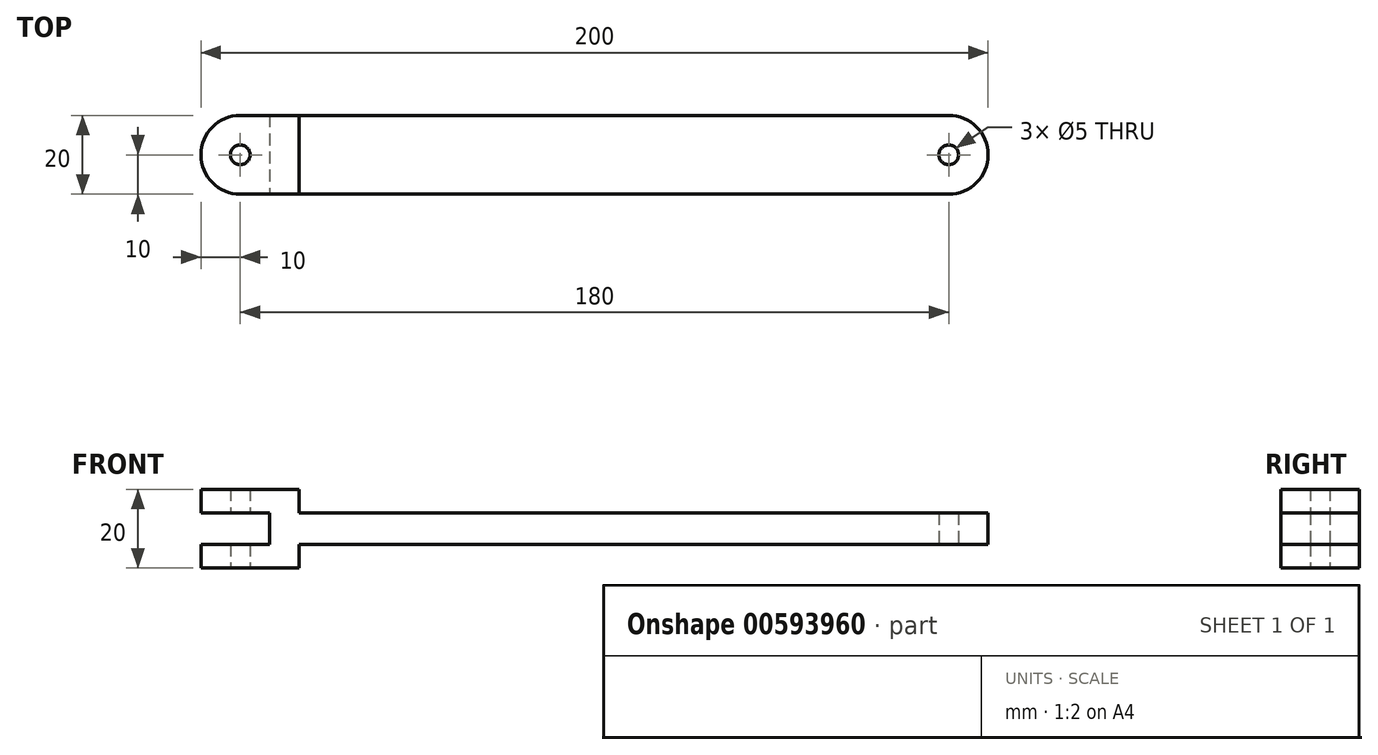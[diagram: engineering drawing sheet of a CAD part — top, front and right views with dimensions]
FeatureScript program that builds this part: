
annotation { "Feature Type Name" : "Feature", "Feature Type Description" : "" }
export const myFeature = defineFeature(function(context is Context, id is Id, definition is map)
    precondition{}
    {
        {
            var Q0;
            Q0=qCreatedBy(makeId("Top.planeOp"),FACE);
            var sketch = newSketch(context, id + "F0", { "sketchPlane" : qUnion([Q0])});
            skLineSegment(sketch, "E0.bottom", {"start": v(75, 10) * mm, "end": v(-75, 10) * mm});
            skLineSegment(sketch, "E0.top", {"start": v(75, -10) * mm, "end": v(-75, -10) * mm});
            skLineSegment(sketch, "E0.left", {"start": v(75, 10) * mm, "end": v(75, -10) * mm});
            skLineSegment(sketch, "E0.right", {"start": v(-75, 10) * mm, "end": v(-75, -10) * mm});
            skPoint(sketch, "E0.middle", {"position": v(0, 0) * mm});
            skCircle(sketch, "E1", {"center": v(90, 0) * mm, "radius": 10 * mm});
            skPoint(sketch, "E2", {"position": v(100, 0) * mm});
            skPoint(sketch, "E3", {"position": v(90, 10) * mm});
            skPoint(sketch, "E4", {"position": v(90, -10) * mm});
            skLineSegment(sketch, "E5", {"start": v(75, 10) * mm, "end": v(90, 10) * mm});
            skLineSegment(sketch, "E6", {"start": v(90, -10) * mm, "end": v(75, -10) * mm});
            skCircle(sketch, "E7", {"center": v(90, 0) * mm, "radius": 2.5 * mm});
            skCircle(sketch, "E8", {"center": v(-90, 0) * mm, "radius": 10 * mm});
            skPoint(sketch, "E9", {"position": v(-100, 0) * mm});
            skLineSegment(sketch, "E10", {"start": v(-90, 0) * mm, "end": v(-90, 10) * mm, "construction": true});
            skLineSegment(sketch, "E11", {"start": v(-90, 10) * mm, "end": v(-90, 0) * mm, "construction": true});
            skLineSegment(sketch, "E12", {"start": v(-90, -10) * mm, "end": v(-90, 0) * mm, "construction": true});
            skLineSegment(sketch, "E13", {"start": v(-90, 0) * mm, "end": v(-100, 0) * mm, "construction": true});
            skLineSegment(sketch, "E14", {"start": v(-90, 0) * mm, "end": v(-75, 0) * mm, "construction": true});
            skLineSegment(sketch, "E15", {"start": v(-90, 10) * mm, "end": v(-75, 10) * mm});
            skLineSegment(sketch, "E16", {"start": v(-90, -10) * mm, "end": v(-75, -10) * mm});
            skLineSegment(sketch, "E17", {"start": v(-75, -10) * mm, "end": v(-75, 10) * mm});
            skCircle(sketch, "E18", {"center": v(-90, 0) * mm, "radius": 2.5 * mm});
            skSolve(sketch);
        }
        {
            var Q0;
            Q0=makeQuery(id+"F0.imprint","IMPRINT",FACE,{"disambiguationData":[TD([[makeQuery(id+"F0.imprint","IMPRINT",EDGE,{"derivedFrom":sQuery(id+"F0.wireOp",EDGE,"E0.bottom")}),1.0]])]});
            var Q1;
            Q1=makeQuery(id+"F0.imprint","IMPRINT",FACE,{"disambiguationData":[TD([[makeQuery(id+"F0.imprint","IMPRINT",EDGE,{"derivedFrom":sQuery(id+"F0.wireOp",EDGE,"E0.left")}),1.0]])]});
            var Q2;
            Q2=makeQuery(id+"F0.imprint","IMPRINT",FACE,{"disambiguationData":[TD([[makeQuery(id+"F0.imprint","IMPRINT",EDGE,{"derivedFrom":sQuery(id+"F0.wireOp",EDGE,"E7")}),-1.0]])]});
            var Q3;
            Q3=makeQuery(id+"F0.imprint","IMPRINT",FACE,{"disambiguationData":[TD([[makeQuery(id+"F0.imprint","IMPRINT",EDGE,{"derivedFrom":sQuery(id+"F0.wireOp",EDGE,"5iIiheSA-0ZHN-F9So-mZuT-hha1FEnrlhel.bottom")}),1.0]])]});
            extrude(context, id + "F1", {"entities" : qUnion([Q0, Q1, Q2, Q3]), "endBound" : BoundingType.SYMMETRIC, "depth" : 8 * mm, "offsetDistance" : 25 * mm});
        }
        {
            var Q0;
            Q0=makeQuery(id+"F0.imprint","IMPRINT",FACE,{"disambiguationData":[TD([[makeQuery(id+"F0.imprint","IMPRINT",EDGE,{"derivedFrom":sQuery(id+"F0.wireOp",EDGE,"E18")}),-1.0]])]});
            var Q1;
            {var subQ0=sQuery(id+"F0.wireOp",EDGE,"E15");Q1=makeQuery(id+"F0.imprint","IMPRINT",FACE,{"disambiguationData":[TD([[makeQuery(id+"F0.imprint","IMPRINT",EDGE,{"derivedFrom":subQ0}),-1.0]])]});}
            extrude(context, id + "F2", {"entities" : qUnion([Q0, Q1]), "operationType" : NewBodyOperationType.ADD, "endBound" : BoundingType.SYMMETRIC, "depth" : 20 * mm, "offsetDistance" : 25 * mm});
        }
        {
            var Q0;
            Q0=makeQuery(id+"F2.boolean.opBoolean","MERGE",FACE,{"derivedFrom":[makeQuery(id+"F1.opExtrude","SWEPT_FACE",FACE,{"disambiguationData":[OSD([sQuery(id+"F0.wireOp",EDGE,"E0.top"),sQuery(id+"F0.wireOp",EDGE,"E6")])]}),makeQuery(id+"F2.opExtrude","SWEPT_FACE",FACE,{"disambiguationData":[OSD([sQuery(id+"F0.wireOp",EDGE,"E16")])]})]});
            var sketch = newSketch(context, id + "F3", { "sketchPlane" : qUnion([Q0])});
            skLineSegment(sketch, "E19", {"start": v(-82.5, 10) * mm, "end": v(-82.5, -10) * mm, "construction": true});
            skLineSegment(sketch, "E20", {"start": v(-75, 4) * mm, "end": v(-82.5, 4) * mm, "construction": true});
            skLineSegment(sketch, "E21", {"start": v(-75, -4) * mm, "end": v(-82.5, -4) * mm, "construction": true});
            skLineSegment(sketch, "E22.bottom", {"start": v(-82.5, 4) * mm, "end": v(-100.55, 4) * mm});
            skLineSegment(sketch, "E22.top", {"start": v(-82.5, -4) * mm, "end": v(-100.55, -4) * mm});
            skLineSegment(sketch, "E22.left", {"start": v(-82.5, 4) * mm, "end": v(-82.5, -4) * mm});
            skLineSegment(sketch, "E22.right", {"start": v(-100.55, 4) * mm, "end": v(-100.55, -4) * mm});
            skSolve(sketch);
        }
        {
            var Q0;
            {var subQ0=sQuery(id+"F3.wireOp",EDGE,"E22.left");Q0=makeQuery(id+"F3.imprint","IMPRINT",FACE,{"disambiguationData":[TD([[makeQuery(id+"F3.imprint","IMPRINT",EDGE,{"derivedFrom":subQ0}),-1.0]])]});}
            var Q1;
            {var subQ0=sQuery(id+"F3.wireOp",EDGE,"E22.right");Q1=makeQuery(id+"F3.imprint","IMPRINT",FACE,{"disambiguationData":[TD([[makeQuery(id+"F3.imprint","IMPRINT",EDGE,{"derivedFrom":subQ0}),1.0]])]});}
            extrude(context, id + "F4", {"entities" : qUnion([Q0, Q1]), "operationType" : NewBodyOperationType.REMOVE, "oppositeDirection" : true, "depth" : 25 * mm, "offsetDistance" : 25 * mm});
        }
    });
